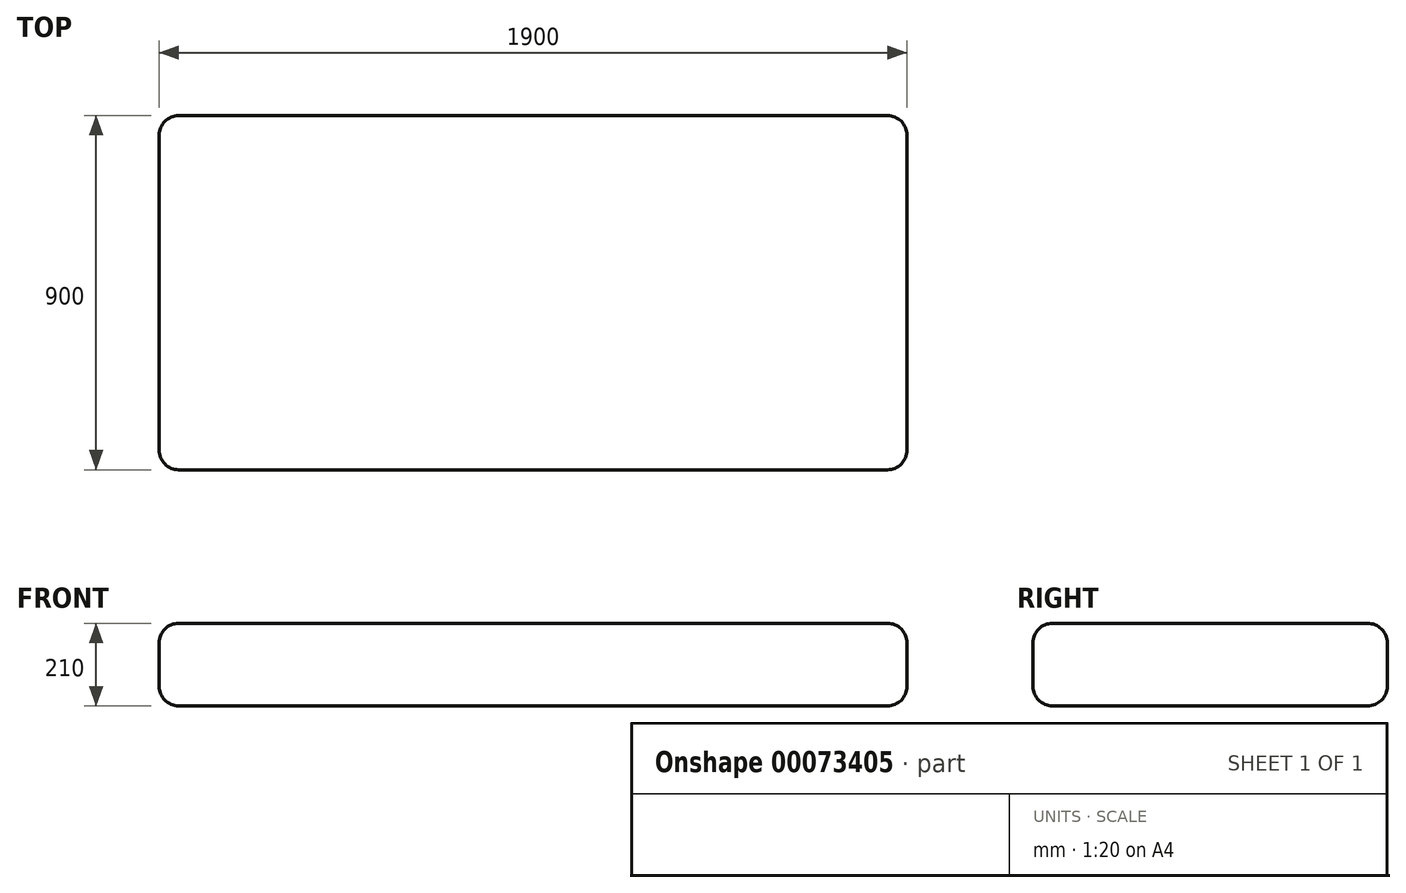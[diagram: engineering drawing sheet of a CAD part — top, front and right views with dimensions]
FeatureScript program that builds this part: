
annotation { "Feature Type Name" : "Feature", "Feature Type Description" : "" }
export const myFeature = defineFeature(function(context is Context, id is Id, definition is map)
    precondition{}
    {
        {
            var Q0;
            Q0=qCreatedBy(makeId("Top.planeOp"),FACE);
            var sketch = newSketch(context, id + "F0", { "sketchPlane" : qUnion([Q0])});
            skLineSegment(sketch, "E0.rect.bottom", {"start": v(950, 450) * mm, "end": v(-950, 450) * mm});
            skLineSegment(sketch, "E0.rect.top", {"start": v(950, -450) * mm, "end": v(-950, -450) * mm});
            skLineSegment(sketch, "E0.rect.left", {"start": v(950, 450) * mm, "end": v(950, -450) * mm});
            skLineSegment(sketch, "E0.rect.right", {"start": v(-950, 450) * mm, "end": v(-950, -450) * mm});
            skPoint(sketch, "E0.rect.middle", {"position": v(0, 0) * mm});
            skSolve(sketch);
        }
        {
            var Q0;
            Q0=makeQuery(id+"F0.imprint","IMPRINT",FACE,{"disambiguationData":[TD([[makeQuery(id+"F0.imprint","IMPRINT",EDGE,{"derivedFrom":sQuery(id+"F0.wireOp",EDGE,"E0.rect.bottom")}),1.0]])]});
            extrude(context, id + "F1", {"entities" : qUnion([Q0]), "depth" : 210 * mm});
        }
        {
            var Q0;
            Q0=makeQuery(id+"F1.opExtrude","SWEPT_EDGE",EDGE,{"disambiguationData":[OSD([sQuery(id+"F0.wireOp",EDGE,"E0.rect.bottom"),sQuery(id+"F0.wireOp",EDGE,"E0.rect.right")])]});
            var Q1;
            Q1=makeQuery(id+"F1.opExtrude","SWEPT_EDGE",EDGE,{"disambiguationData":[OSD([sQuery(id+"F0.wireOp",EDGE,"E0.rect.top"),sQuery(id+"F0.wireOp",EDGE,"E0.rect.right")])]});
            var Q2;
            Q2=makeQuery(id+"F1.opExtrude","SWEPT_EDGE",EDGE,{"disambiguationData":[OSD([sQuery(id+"F0.wireOp",EDGE,"E0.rect.top"),sQuery(id+"F0.wireOp",EDGE,"E0.rect.left")])]});
            var Q3;
            Q3=makeQuery(id+"F1.opExtrude","SWEPT_EDGE",EDGE,{"disambiguationData":[OSD([sQuery(id+"F0.wireOp",EDGE,"E0.rect.bottom"),sQuery(id+"F0.wireOp",EDGE,"E0.rect.left")])]});
            fillet(context, id + "F2", {"entities" : qUnion([Q0, Q1, Q2, Q3]), "radius" : 50 * mm, "tangentPropagation" : true, "allowEdgeOverflow" : false});
        }
        {
            var Q0;
            Q0=makeQuery(id+"F1.opExtrude","CAP_EDGE",EDGE,{"disambiguationData":[OSD([sQuery(id+"F0.wireOp",EDGE,"E0.rect.top")])],"isStart":false});
            var Q1;
            Q1=makeQuery(id+"F1.opExtrude","CAP_EDGE",EDGE,{"disambiguationData":[OSD([sQuery(id+"F0.wireOp",EDGE,"E0.rect.top")])],"isStart":true});
            fillet(context, id + "F3", {"entities" : qUnion([Q0, Q1]), "radius" : 50 * mm, "tangentPropagation" : true, "allowEdgeOverflow" : false});
        }
    });
